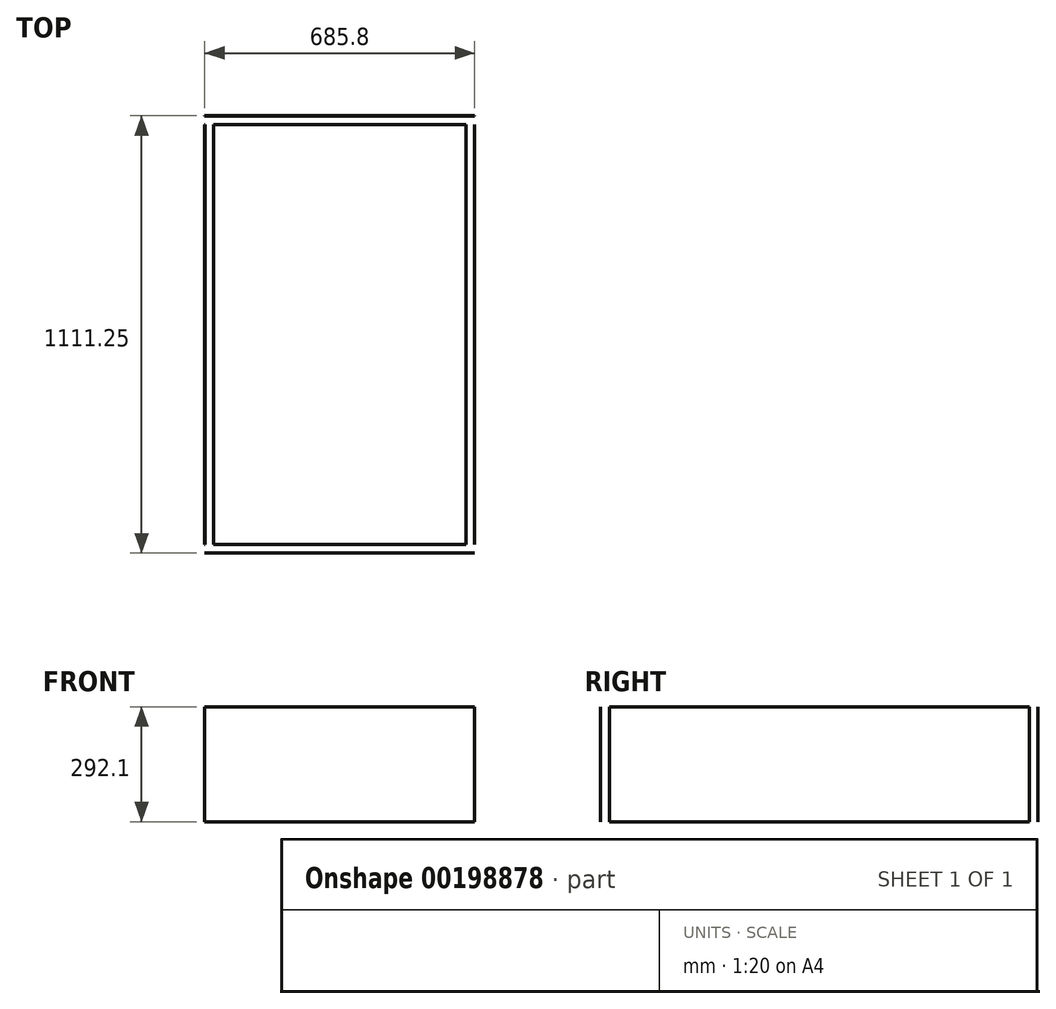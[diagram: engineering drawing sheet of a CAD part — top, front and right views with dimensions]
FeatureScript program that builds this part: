
annotation { "Feature Type Name" : "Feature", "Feature Type Description" : "" }
export const myFeature = defineFeature(function(context is Context, id is Id, definition is map)
    precondition{}
    {
        {
            assignVariable(context, id + "F0", {"name" : "x", "anyValue" : 7 / 8});
        }
        {
            var Q0;
            Q0=qCreatedBy(makeId("Front.planeOp"),FACE);
            var sketch = newSketch(context, id + "F1", { "sketchPlane" : qUnion([Q0])});
            skLineSegment(sketch, "E0.bottom", {"start": v(-342.9, 292.1) * mm, "end": v(342.9, 292.1) * mm});
            skLineSegment(sketch, "E0.top", {"start": v(-342.9, 0) * mm, "end": v(342.9, 0) * mm});
            skLineSegment(sketch, "E0.left", {"start": v(-342.9, 292.1) * mm, "end": v(-342.9, 0) * mm});
            skLineSegment(sketch, "E0.right", {"start": v(342.9, 292.1) * mm, "end": v(342.9, 0) * mm});
            skSolve(sketch);
        }
        {
            var Q0;
            Q0 = qSketchRegion(id + "F1", true);
            extrude(context, id + "F2", {"entities" : qUnion([Q0]), "oppositeDirection" : true, "depth" : 7 / 203.2 * mm});
        }
        {
            var Q0;
            Q0=makeQuery(id+"F2.opExtrude","SWEPT_FACE",FACE,{"disambiguationData":[OSD([sQuery(id+"F1.wireOp",EDGE,"E0.top")])]});
            var sketch = newSketch(context, id + "F3", { "sketchPlane" : qUnion([Q0])});
            skLineSegment(sketch, "E1.bottom", {"start": v(-320.68, -22.23) * mm, "end": v(320.67, -22.23) * mm});
            skLineSegment(sketch, "E1.top", {"start": v(-320.68, -1089.02) * mm, "end": v(320.68, -1089.02) * mm});
            skLineSegment(sketch, "E1.left", {"start": v(-320.68, -22.22) * mm, "end": v(-320.68, -1089.02) * mm});
            skLineSegment(sketch, "E1.right", {"start": v(320.68, -22.22) * mm, "end": v(320.68, -1089.02) * mm});
            skLineSegment(sketch, "E2", {"start": v(0, -22.23) * mm, "end": v(0, 0) * mm, "construction": true});
            skSolve(sketch);
        }
        {
            var Q0;
            Q0 = qSketchRegion(id + "F3", true);
            extrude(context, id + "F4", {"entities" : qUnion([Q0]), "oppositeDirection" : true, "depth" : (getVariable(context, 'x')) * mm});
        }
        {
            var Q0;
            Q0=makeQuery(id+"F2.opExtrude","SWEPT_FACE",FACE,{"disambiguationData":[OSD([sQuery(id+"F1.wireOp",EDGE,"E0.right")])]});
            var sketch = newSketch(context, id + "F5", { "sketchPlane" : qUnion([Q0])});
            skLineSegment(sketch, "E3.bottom", {"start": v(22.22, 292.1) * mm, "end": v(1089.02, 292.1) * mm});
            skLineSegment(sketch, "E4", {"start": v(22.22, 0) * mm, "end": v(22.22, 292.1) * mm});
            skLineSegment(sketch, "E5", {"start": v(1089.02, 292.1) * mm, "end": v(1089.02, 0) * mm});
            skLineSegment(sketch, "E6", {"start": v(1089.02, 0) * mm, "end": v(22.23, 0) * mm});
            skSolve(sketch);
        }
        {
            var Q0;
            Q0 = qSketchRegion(id + "F5", true);
            var Q1;
            Q1 = qConstructionFilter(qBodyType(qCreatedBy(id + "F5" ,EDGE), BodyType.WIRE), ConstructionObject.NO);
            extrude(context, id + "F6", {"entities" : qUnion([Q0]), "surfaceEntities" : qUnion([Q1]), "oppositeDirection" : true, "depth" : (getVariable(context, 'x')) * mm});
        }
        {
            var Q0;
            Q0=makeQuery(id+"F6.opExtrude","SWEPT_BODY",BODY,{"disambiguationData":[OSD([sQuery(id+"F5.wireOp",EDGE,"E3.bottom"),sQuery(id+"F5.wireOp",EDGE,"E3.top"),sQuery(id+"F5.wireOp",EDGE,"E3.left"),sQuery(id+"F5.wireOp",EDGE,"E3.right")])]});
            var Q1;
            Q1=qCreatedBy(makeId("Right.planeOp"),FACE);
            mirror(context, id + "F7", {"entities" : qUnion([Q0]), "mirrorPlane" : qUnion([Q1])});
        }
        {
            var Q0;
            Q0=makeQuery(id+"F6.opExtrude","SWEPT_FACE",FACE,{"disambiguationData":[OSD([sQuery(id+"F5.wireOp",EDGE,"E4")])]});
            var Q1;
            Q1=makeQuery(id+"F6.opExtrude","SWEPT_FACE",FACE,{"disambiguationData":[OSD([sQuery(id+"F5.wireOp",EDGE,"E5")])]});
            cPlane(context, id + "F8", {"entities" : qUnion([Q0, Q1]), "cplaneType" : CPlaneType.MID_PLANE, "offset" : 25.4 * mm, "width" : 152.4 * mm, "height" : 152.4 * mm});
        }
        {
            var Q0;
            Q0=makeQuery(id+"F2.opExtrude","SWEPT_BODY",BODY,{"disambiguationData":[OSD([sQuery(id+"F1.wireOp",EDGE,"E0.bottom"),sQuery(id+"F1.wireOp",EDGE,"E0.top"),sQuery(id+"F1.wireOp",EDGE,"E0.left"),sQuery(id+"F1.wireOp",EDGE,"E0.right")])]});
            var Q1;
            Q1=qCreatedBy(id+"F8.planeOp",FACE);
            mirror(context, id + "F9", {"entities" : qUnion([Q0]), "mirrorPlane" : qUnion([Q1])});
        }
    });
